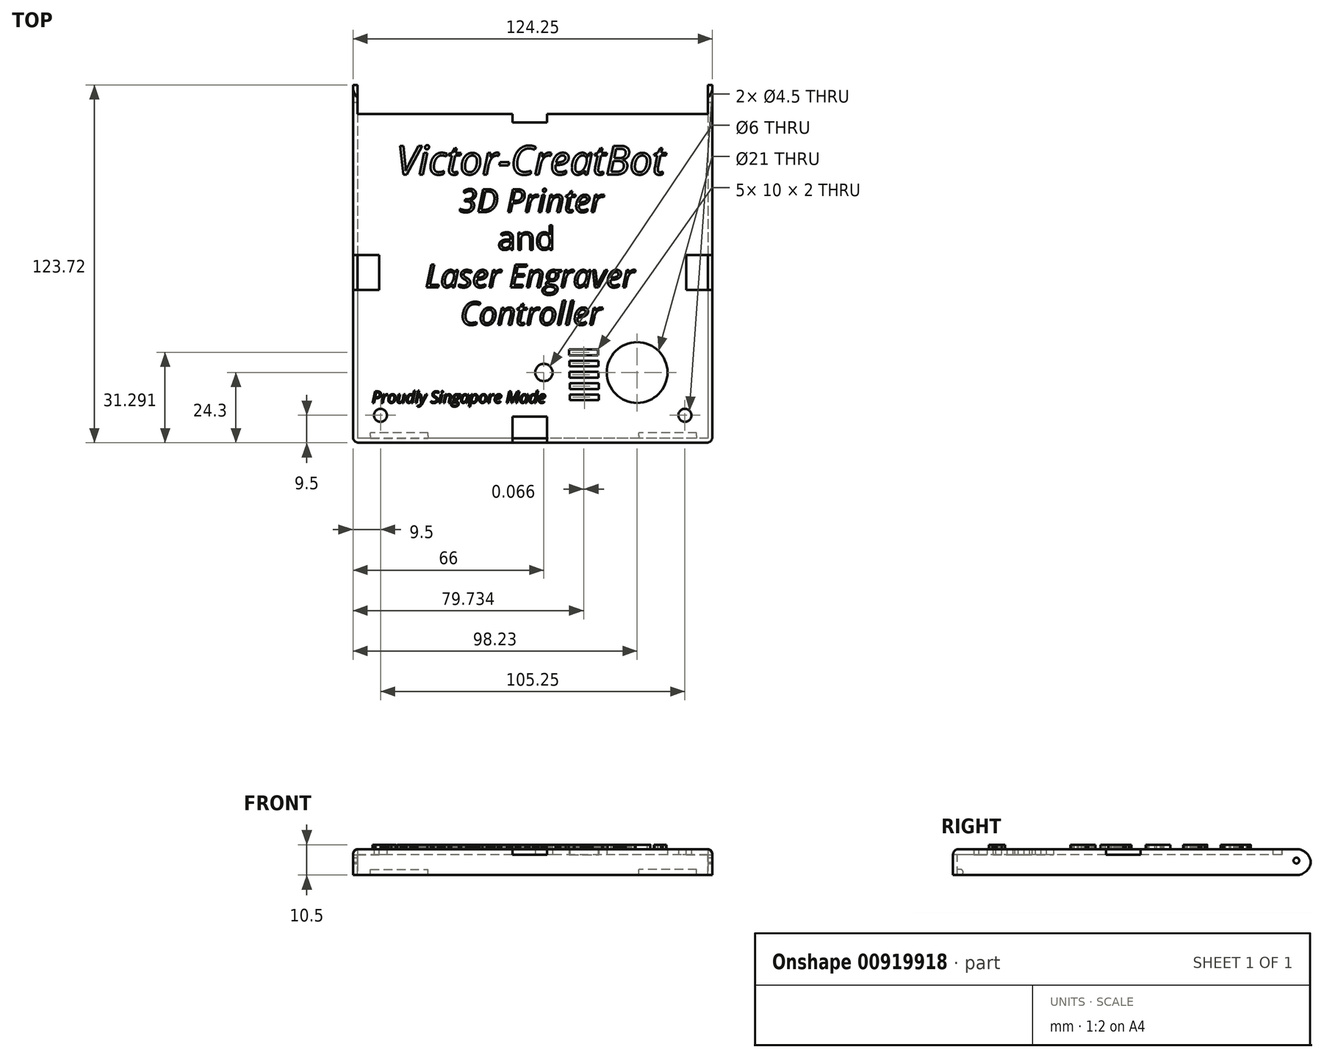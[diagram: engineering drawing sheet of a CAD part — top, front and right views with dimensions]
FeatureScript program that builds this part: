
annotation { "Feature Type Name" : "Feature", "Feature Type Description" : "" }
export const myFeature = defineFeature(function(context is Context, id is Id, definition is map)
    precondition{}
    {
        {
            var Q0;
            Q0=qCreatedBy(makeId("Top.planeOp"),FACE);
            var sketch = newSketch(context, id + "F0", { "sketchPlane" : qUnion([Q0])});
            skLineSegment(sketch, "E0.bottom", {"start": v(0, 0) * mm, "end": v(112.25, 0) * mm});
            skLineSegment(sketch, "E0.top", {"start": v(0, 107.75) * mm, "end": v(112.25, 107.75) * mm});
            skLineSegment(sketch, "E0.left", {"start": v(0, 0) * mm, "end": v(0, 107.75) * mm});
            skLineSegment(sketch, "E0.right", {"start": v(112.25, 0) * mm, "end": v(112.25, 107.75) * mm});
            skCircle(sketch, "E1", {"center": v(3.5, 3.5) * mm, "radius": 2.25 * mm});
            skCircle(sketch, "E2", {"center": v(108.75, 3.5) * mm, "radius": 2.25 * mm});
            skCircle(sketch, "E3", {"center": v(92.23, 18.3) * mm, "radius": 10.5 * mm});
            skCircle(sketch, "E4", {"center": v(60, 18.3) * mm, "radius": 3 * mm});
            skLineSegment(sketch, "E5.bottom", {"start": v(68.73, 26.3) * mm, "end": v(78.73, 26.3) * mm});
            skLineSegment(sketch, "E5.top", {"start": v(68.73, 24.3) * mm, "end": v(78.73, 24.3) * mm});
            skLineSegment(sketch, "E5.left", {"start": v(68.73, 26.3) * mm, "end": v(68.73, 24.3) * mm});
            skLineSegment(sketch, "E5.right", {"start": v(78.73, 26.3) * mm, "end": v(78.73, 24.3) * mm});
            skLineSegment(sketch, "E6.1.0.0", {"start": v(78.8, 22.4) * mm, "end": v(78.8, 20.4) * mm});
            skLineSegment(sketch, "E6.1.0.1", {"start": v(68.8, 22.4) * mm, "end": v(68.8, 20.4) * mm});
            skLineSegment(sketch, "E6.1.0.2", {"start": v(68.8, 22.4) * mm, "end": v(78.8, 22.4) * mm});
            skLineSegment(sketch, "E6.1.0.3", {"start": v(68.8, 20.4) * mm, "end": v(78.8, 20.4) * mm});
            skLineSegment(sketch, "E6.2.0.0", {"start": v(78.87, 18.5) * mm, "end": v(78.87, 16.5) * mm});
            skLineSegment(sketch, "E6.2.0.1", {"start": v(68.87, 18.5) * mm, "end": v(68.87, 16.5) * mm});
            skLineSegment(sketch, "E6.2.0.2", {"start": v(68.87, 18.5) * mm, "end": v(78.87, 18.5) * mm});
            skLineSegment(sketch, "E6.2.0.3", {"start": v(68.87, 16.5) * mm, "end": v(78.87, 16.5) * mm});
            skLineSegment(sketch, "E6.3.0.0", {"start": v(78.93, 14.62) * mm, "end": v(78.93, 12.62) * mm});
            skLineSegment(sketch, "E6.3.0.1", {"start": v(68.93, 14.62) * mm, "end": v(68.93, 12.62) * mm});
            skLineSegment(sketch, "E6.3.0.2", {"start": v(68.93, 14.62) * mm, "end": v(78.93, 14.62) * mm});
            skLineSegment(sketch, "E6.3.0.3", {"start": v(68.93, 12.62) * mm, "end": v(78.93, 12.62) * mm});
            skLineSegment(sketch, "E6.4.0.0", {"start": v(79, 10.73) * mm, "end": v(79, 8.73) * mm});
            skLineSegment(sketch, "E6.4.0.1", {"start": v(69, 10.73) * mm, "end": v(69, 8.73) * mm});
            skLineSegment(sketch, "E6.4.0.2", {"start": v(69, 10.73) * mm, "end": v(79, 10.73) * mm});
            skLineSegment(sketch, "E6.4.0.3", {"start": v(69, 8.73) * mm, "end": v(79, 8.73) * mm});
            skLineSegment(sketch, "E6.direction1", {"start": v(68.73, 24.3) * mm, "end": v(68.8, 20.4) * mm, "construction": true});
            skSolve(sketch);
        }
        {
            var Q0;
            Q0=qSketchRegion(id+"F0",true);
            extrude(context, id + "F1", {"entities" : qUnion([Q0]), "depth" : 2 * mm, "offsetDistance" : 25 * mm});
        }
        {
            var Q0;
            Q0=makeQuery(id+"F1.opExtrude","CAP_FACE",FACE,{"disambiguationData":[OSD([sQuery(id+"F0.wireOp",EDGE,"E0.bottom"),sQuery(id+"F0.wireOp",EDGE,"E0.top"),sQuery(id+"F0.wireOp",EDGE,"E0.left"),sQuery(id+"F0.wireOp",EDGE,"E0.right"),sQuery(id+"F0.wireOp",EDGE,"VJWhoFmN-CNNd-a6gC-JCuR-XAWFigalHExP"),sQuery(id+"F0.wireOp",EDGE,"vIjKD9R8-VXcQ-Syzh-FnhK-4sEpH6Cil4JO"),sQuery(id+"F0.wireOp",EDGE,"E1"),sQuery(id+"F0.wireOp",EDGE,"E2"),sQuery(id+"F0.wireOp",EDGE,"RQaqiYP4-0Fcv-lfBv-gB3g-qDtZXz7Vt3Ng.bottom"),sQuery(id+"F0.wireOp",EDGE,"RQaqiYP4-0Fcv-lfBv-gB3g-qDtZXz7Vt3Ng.top"),sQuery(id+"F0.wireOp",EDGE,"RQaqiYP4-0Fcv-lfBv-gB3g-qDtZXz7Vt3Ng.left"),sQuery(id+"F0.wireOp",EDGE,"RQaqiYP4-0Fcv-lfBv-gB3g-qDtZXz7Vt3Ng.right"),sQuery(id+"F0.wireOp",EDGE,"E3"),sQuery(id+"F0.wireOp",EDGE,"E4"),sQuery(id+"F0.wireOp",EDGE,"A4T1cfBq-erl5-skMh-XZ60-SgpOEBQzwWt8"),sQuery(id+"F0.wireOp",EDGE,"E5.bottom"),sQuery(id+"F0.wireOp",EDGE,"E5.top"),sQuery(id+"F0.wireOp",EDGE,"E5.left"),sQuery(id+"F0.wireOp",EDGE,"E5.right"),sQuery(id+"F0.wireOp",EDGE,"E6.1.0.0"),sQuery(id+"F0.wireOp",EDGE,"E6.1.0.1"),sQuery(id+"F0.wireOp",EDGE,"E6.1.0.2"),sQuery(id+"F0.wireOp",EDGE,"E6.1.0.3"),sQuery(id+"F0.wireOp",EDGE,"E6.2.0.0"),sQuery(id+"F0.wireOp",EDGE,"E6.2.0.1"),sQuery(id+"F0.wireOp",EDGE,"E6.2.0.2"),sQuery(id+"F0.wireOp",EDGE,"E6.2.0.3"),sQuery(id+"F0.wireOp",EDGE,"E6.3.0.0"),sQuery(id+"F0.wireOp",EDGE,"E6.3.0.1"),sQuery(id+"F0.wireOp",EDGE,"E6.3.0.2"),sQuery(id+"F0.wireOp",EDGE,"E6.3.0.3"),sQuery(id+"F0.wireOp",EDGE,"E6.4.0.0"),sQuery(id+"F0.wireOp",EDGE,"E6.4.0.1"),sQuery(id+"F0.wireOp",EDGE,"E6.4.0.2"),sQuery(id+"F0.wireOp",EDGE,"E6.4.0.3")])],"isStart":false});
            var sketch = newSketch(context, id + "F2", { "sketchPlane" : qUnion([Q0])});
            skLineSegment(sketch, "E7.bottom", {"start": v(109.25, 58.87) * mm, "end": v(115.25, 58.87) * mm});
            skLineSegment(sketch, "E7.top", {"start": v(109.25, 46.87) * mm, "end": v(115.25, 46.87) * mm});
            skLineSegment(sketch, "E7.left", {"start": v(109.25, 58.87) * mm, "end": v(109.25, 46.87) * mm});
            skLineSegment(sketch, "E7.right", {"start": v(115.25, 58.87) * mm, "end": v(115.25, 46.87) * mm});
            skLineSegment(sketch, "E8.bottom", {"start": v(-3, 58.87) * mm, "end": v(3, 58.87) * mm});
            skLineSegment(sketch, "E8.top", {"start": v(-3, 46.87) * mm, "end": v(3, 46.87) * mm});
            skLineSegment(sketch, "E8.left", {"start": v(-3, 58.87) * mm, "end": v(-3, 46.87) * mm});
            skLineSegment(sketch, "E8.right", {"start": v(3, 58.87) * mm, "end": v(3, 46.87) * mm});
            skLineSegment(sketch, "E9.bottom", {"start": v(49.13, 110.75) * mm, "end": v(61.13, 110.75) * mm});
            skLineSegment(sketch, "E9.top", {"start": v(49.13, 104.75) * mm, "end": v(61.13, 104.75) * mm});
            skLineSegment(sketch, "E9.left", {"start": v(49.13, 110.75) * mm, "end": v(49.13, 104.75) * mm});
            skLineSegment(sketch, "E9.right", {"start": v(61.13, 110.75) * mm, "end": v(61.13, 104.75) * mm});
            skLineSegment(sketch, "E10.bottom", {"start": v(49.13, 3) * mm, "end": v(61.13, 3) * mm});
            skLineSegment(sketch, "E10.top", {"start": v(49.13, -3) * mm, "end": v(61.13, -3) * mm});
            skLineSegment(sketch, "E10.left", {"start": v(49.13, 3) * mm, "end": v(49.13, -3) * mm});
            skLineSegment(sketch, "E10.right", {"start": v(61.13, 3) * mm, "end": v(61.13, -3) * mm});
            skSolve(sketch);
        }
        {
            var Q0;
            Q0=qSketchRegion(id+"F2",true);
            extrude(context, id + "F3", {"entities" : qUnion([Q0]), "operationType" : NewBodyOperationType.REMOVE, "endBound" : BoundingType.THROUGH_ALL, "oppositeDirection" : true, "depth" : 3 * mm, "offsetDistance" : 25 * mm});
        }
        {
            var Q0;
            {var subQ27=sQuery(id+"F0.wireOp",EDGE,"E0.left");var subQ29=sQuery(id+"F0.wireOp",EDGE,"E0.bottom");Q0=makeQuery(id+"F3.boolean.opBoolean","SPLIT",FACE,{"disambiguationData":[TD([makeQuery(id+"F1.opExtrude","SWEPT_FACE",FACE,{"disambiguationData":[OSD([subQ27])]})])],"derivedFrom":makeQuery(id+"F1.opExtrude","SWEPT_FACE",FACE,{"disambiguationData":[OSD([subQ29])]})});}
            var Q1;
            {var subQ26=sQuery(id+"F0.wireOp",EDGE,"E0.right");var subQ29=sQuery(id+"F0.wireOp",EDGE,"E0.bottom");Q1=makeQuery(id+"F3.boolean.opBoolean","SPLIT",FACE,{"disambiguationData":[TD([makeQuery(id+"F1.opExtrude","SWEPT_FACE",FACE,{"disambiguationData":[OSD([subQ26])]})])],"derivedFrom":makeQuery(id+"F1.opExtrude","SWEPT_FACE",FACE,{"disambiguationData":[OSD([subQ29])]})});}
            extrude(context, id + "F4", {"entities" : qUnion([Q0, Q1]), "operationType" : NewBodyOperationType.ADD, "depth" : 6 * mm, "offsetDistance" : 25 * mm});
        }
        {
            var Q0;
            {var subQ27=sQuery(id+"F0.wireOp",EDGE,"E0.left");var subQ28=sQuery(id+"F0.wireOp",EDGE,"E0.top");Q0=makeQuery(id+"F3.boolean.opBoolean","SPLIT",FACE,{"disambiguationData":[TD([makeQuery(id+"F1.opExtrude","SWEPT_FACE",FACE,{"disambiguationData":[OSD([subQ28])]})])],"derivedFrom":makeQuery(id+"F1.opExtrude","SWEPT_FACE",FACE,{"disambiguationData":[OSD([subQ27])]})});}
            var Q1;
            {var subQ0=sQuery(id+"F0.wireOp",EDGE,"E0.left");var subQ1=sQuery(id+"F0.wireOp",EDGE,"E0.bottom");Q1=makeQuery(id+"F4.boolean.opBoolean","MERGE",FACE,{"derivedFrom":[makeQuery(id+"F3.boolean.opBoolean","SPLIT",FACE,{"disambiguationData":[TD([makeQuery(id+"F1.opExtrude","SWEPT_FACE",FACE,{"disambiguationData":[OSD([subQ1])]})])],"derivedFrom":makeQuery(id+"F1.opExtrude","SWEPT_FACE",FACE,{"disambiguationData":[OSD([subQ0])]})}),makeQuery(id+"F4.opExtrude","SWEPT_FACE",FACE,{"disambiguationData":[OSD([subQ1,subQ0])]})]});}
            extrude(context, id + "F5", {"entities" : qUnion([Q0, Q1]), "operationType" : NewBodyOperationType.ADD, "depth" : 6 * mm, "offsetDistance" : 25 * mm});
        }
        {
            var Q0;
            {var subQ26=sQuery(id+"F0.wireOp",EDGE,"E0.right");var subQ28=sQuery(id+"F0.wireOp",EDGE,"E0.top");Q0=makeQuery(id+"F3.boolean.opBoolean","SPLIT",FACE,{"disambiguationData":[TD([makeQuery(id+"F1.opExtrude","SWEPT_FACE",FACE,{"disambiguationData":[OSD([subQ28])]})])],"derivedFrom":makeQuery(id+"F1.opExtrude","SWEPT_FACE",FACE,{"disambiguationData":[OSD([subQ26])]})});}
            var Q1;
            {var subQ0=sQuery(id+"F0.wireOp",EDGE,"E0.right");var subQ1=sQuery(id+"F0.wireOp",EDGE,"E0.bottom");Q1=makeQuery(id+"F4.boolean.opBoolean","MERGE",FACE,{"derivedFrom":[makeQuery(id+"F3.boolean.opBoolean","SPLIT",FACE,{"disambiguationData":[TD([makeQuery(id+"F1.opExtrude","SWEPT_FACE",FACE,{"disambiguationData":[OSD([subQ1])]})])],"derivedFrom":makeQuery(id+"F1.opExtrude","SWEPT_FACE",FACE,{"disambiguationData":[OSD([subQ0])]})}),makeQuery(id+"F4.opExtrude","SWEPT_FACE",FACE,{"disambiguationData":[OSD([subQ1,subQ0])]})]});}
            extrude(context, id + "F6", {"entities" : qUnion([Q0, Q1]), "operationType" : NewBodyOperationType.ADD, "depth" : 6 * mm, "offsetDistance" : 25 * mm});
        }
        {
            var Q0;
            {var subQ0=sQuery(id+"F0.wireOp",EDGE,"E0.right");var subQ1=sQuery(id+"F0.wireOp",EDGE,"E0.bottom");var subQ2=makeQuery(id+"F1.opExtrude","SWEPT_FACE",FACE,{"disambiguationData":[OSD([subQ1])]});var subQ3=makeQuery(id+"F1.opExtrude","SWEPT_FACE",FACE,{"disambiguationData":[OSD([subQ0])]});var subQ4=sQuery(id+"F0.wireOp",EDGE,"E0.left");var subQ5=sQuery(id+"F0.wireOp",EDGE,"E0.top");var subQ6=makeQuery(id+"F1.opExtrude","CAP_FACE",FACE,{"disambiguationData":[OSD([subQ1,subQ5,subQ4,subQ0,sQuery(id+"F0.wireOp",EDGE,"VJWhoFmN-CNNd-a6gC-JCuR-XAWFigalHExP"),sQuery(id+"F0.wireOp",EDGE,"vIjKD9R8-VXcQ-Syzh-FnhK-4sEpH6Cil4JO"),sQuery(id+"F0.wireOp",EDGE,"E1"),sQuery(id+"F0.wireOp",EDGE,"E2"),sQuery(id+"F0.wireOp",EDGE,"E3"),sQuery(id+"F0.wireOp",EDGE,"E4"),sQuery(id+"F0.wireOp",EDGE,"E5.bottom"),sQuery(id+"F0.wireOp",EDGE,"E5.top"),sQuery(id+"F0.wireOp",EDGE,"E5.left"),sQuery(id+"F0.wireOp",EDGE,"E5.right"),sQuery(id+"F0.wireOp",EDGE,"E6.1.0.0"),sQuery(id+"F0.wireOp",EDGE,"E6.1.0.1"),sQuery(id+"F0.wireOp",EDGE,"E6.1.0.2"),sQuery(id+"F0.wireOp",EDGE,"E6.1.0.3"),sQuery(id+"F0.wireOp",EDGE,"E6.2.0.0"),sQuery(id+"F0.wireOp",EDGE,"E6.2.0.1"),sQuery(id+"F0.wireOp",EDGE,"E6.2.0.2"),sQuery(id+"F0.wireOp",EDGE,"E6.2.0.3"),sQuery(id+"F0.wireOp",EDGE,"E6.3.0.0"),sQuery(id+"F0.wireOp",EDGE,"E6.3.0.1"),sQuery(id+"F0.wireOp",EDGE,"E6.3.0.2"),sQuery(id+"F0.wireOp",EDGE,"E6.3.0.3"),sQuery(id+"F0.wireOp",EDGE,"E6.4.0.0"),sQuery(id+"F0.wireOp",EDGE,"E6.4.0.1"),sQuery(id+"F0.wireOp",EDGE,"E6.4.0.2"),sQuery(id+"F0.wireOp",EDGE,"E6.4.0.3")])],"isStart":true});var subQ7=makeQuery(id+"F1.opExtrude","CAP_EDGE",EDGE,{"disambiguationData":[OSD([subQ0])],"isStart":true});var subQ8=makeQuery(id+"F1.opExtrude","SWEPT_FACE",FACE,{"disambiguationData":[OSD([subQ5])]});var subQ9=makeQuery(id+"F1.opExtrude","SWEPT_FACE",FACE,{"disambiguationData":[OSD([subQ4])]});var subQ10=makeQuery(id+"F1.opExtrude","CAP_EDGE",EDGE,{"disambiguationData":[OSD([subQ4])],"isStart":true});var subQ11=makeQuery(id+"F1.opExtrude","CAP_EDGE",EDGE,{"disambiguationData":[OSD([subQ1])],"isStart":true});Q0=makeQuery(id+"F6.boolean.opBoolean","MERGE",FACE,{"derivedFrom":[makeQuery(id+"F5.boolean.opBoolean","MERGE",FACE,{"derivedFrom":[makeQuery(id+"F4.boolean.opBoolean","MERGE",FACE,{"derivedFrom":[subQ6,makeQuery(id+"F4.opExtrude","SWEPT_FACE",FACE,{"disambiguationData":[OSD([subQ1]),TDD([makeQuery(id+"F3.boolean.opBoolean","SPLIT",EDGE,{"disambiguationData":[TD([subQ9])],"derivedFrom":subQ11})])]}),makeQuery(id+"F4.opExtrude","SWEPT_FACE",FACE,{"disambiguationData":[OSD([subQ1]),TDD([makeQuery(id+"F3.boolean.opBoolean","SPLIT",EDGE,{"disambiguationData":[TD([subQ3])],"derivedFrom":subQ11})])]})]}),makeQuery(id+"F5.opExtrude","SWEPT_FACE",FACE,{"disambiguationData":[OSD([subQ4]),TDD([makeQuery(id+"F3.boolean.opBoolean","SPLIT",EDGE,{"disambiguationData":[TD([subQ8])],"derivedFrom":subQ10})])]}),makeQuery(id+"F5.opExtrude","SWEPT_FACE",FACE,{"disambiguationData":[OSD([subQ1,subQ4]),TDD([makeQuery(id+"F4.boolean.opBoolean","MERGE",EDGE,{"derivedFrom":[makeQuery(id+"F3.boolean.opBoolean","SPLIT",EDGE,{"disambiguationData":[TD([subQ2])],"derivedFrom":subQ10}),makeQuery(id+"F4.opExtrude","SWEPT_EDGE",EDGE,{"disambiguationData":[OSD([subQ1,subQ4]),TDD([makeQuery(id+"F1.opExtrude","CAP_VERTEX",VERTEX,{"disambiguationData":[OSD([subQ1,subQ4])],"isStart":true})])]})]})])]})]}),makeQuery(id+"F6.opExtrude","SWEPT_FACE",FACE,{"disambiguationData":[OSD([subQ0]),TDD([makeQuery(id+"F3.boolean.opBoolean","SPLIT",EDGE,{"disambiguationData":[TD([subQ8])],"derivedFrom":subQ7})])]}),makeQuery(id+"F6.opExtrude","SWEPT_FACE",FACE,{"disambiguationData":[OSD([subQ1,subQ0]),TDD([makeQuery(id+"F4.boolean.opBoolean","MERGE",EDGE,{"derivedFrom":[makeQuery(id+"F3.boolean.opBoolean","SPLIT",EDGE,{"disambiguationData":[TD([subQ2])],"derivedFrom":subQ7}),makeQuery(id+"F4.opExtrude","SWEPT_EDGE",EDGE,{"disambiguationData":[OSD([subQ1,subQ0]),TDD([makeQuery(id+"F1.opExtrude","CAP_VERTEX",VERTEX,{"disambiguationData":[OSD([subQ1,subQ0])],"isStart":true})])]})]})])]})]});}
            var sketch = newSketch(context, id + "F7", { "sketchPlane" : qUnion([Q0])});
            skLineSegment(sketch, "E11.bottom", {"start": v(118.25, -107.75) * mm, "end": v(116.75, -107.75) * mm});
            skLineSegment(sketch, "E11.top", {"start": v(118.25, 6) * mm, "end": v(116.75, 6) * mm});
            skLineSegment(sketch, "E11.left", {"start": v(118.25, -107.75) * mm, "end": v(118.25, -58.87) * mm});
            skLineSegment(sketch, "E11.right", {"start": v(116.75, -107.75) * mm, "end": v(116.75, -58.87) * mm});
            skLineSegment(sketch, "E12.bottom", {"start": v(-6, -107.75) * mm, "end": v(-4.5, -107.75) * mm});
            skLineSegment(sketch, "E12.top", {"start": v(-6, 6) * mm, "end": v(-4.5, 6) * mm});
            skLineSegment(sketch, "E12.left", {"start": v(-6, -107.75) * mm, "end": v(-6, -58.87) * mm});
            skLineSegment(sketch, "E12.right", {"start": v(-4.5, -107.75) * mm, "end": v(-4.5, -58.87) * mm});
            skLineSegment(sketch, "E13.bottom", {"start": v(116.75, 4.5) * mm, "end": v(61.13, 4.5) * mm});
            skLineSegment(sketch, "E13.top", {"start": v(116.75, 6) * mm, "end": v(61.13, 6) * mm});
            skLineSegment(sketch, "E14.trimOffspring", {"start": v(61.13, 4.5) * mm, "end": v(-4.5, 4.5) * mm});
            skLineSegment(sketch, "E15.trimOffspring", {"start": v(61.13, 6) * mm, "end": v(-4.5, 6) * mm});
            skLineSegment(sketch, "E16.trimOffspring", {"start": v(118.25, -58.87) * mm, "end": v(118.25, 6) * mm});
            skLineSegment(sketch, "E17.trimOffspring", {"start": v(116.75, -58.87) * mm, "end": v(116.75, 4.5) * mm});
            skLineSegment(sketch, "E18.trimOffspring", {"start": v(-4.5, -58.87) * mm, "end": v(-4.5, 4.5) * mm});
            skLineSegment(sketch, "E19.trimOffspring", {"start": v(-6, -58.87) * mm, "end": v(-6, 6) * mm});
            skSolve(sketch);
        }
        {
            var Q0;
            {var subQ43=sQuery(id+"F7.wireOp",EDGE,"E12.top");Q0=makeQuery(id+"F7.imprint","IMPRINT",FACE,{"disambiguationData":[TD([[makeQuery(id+"F7.imprint","IMPRINT",EDGE,{"derivedFrom":subQ43}),-1.0]])]});}
            var Q1;
            {var subQ0=sQuery(id+"F7.wireOp",EDGE,"E14.trimOffspring");var subQ2=sQuery(id+"F0.wireOp",EDGE,"E6.4.0.3");var subQ3=sQuery(id+"F0.wireOp",EDGE,"E6.4.0.2");var subQ4=sQuery(id+"F0.wireOp",EDGE,"E6.4.0.1");var subQ5=sQuery(id+"F0.wireOp",EDGE,"E6.4.0.0");var subQ6=sQuery(id+"F0.wireOp",EDGE,"E6.3.0.3");var subQ7=sQuery(id+"F0.wireOp",EDGE,"E6.3.0.2");var subQ8=sQuery(id+"F0.wireOp",EDGE,"E6.3.0.1");var subQ9=sQuery(id+"F0.wireOp",EDGE,"E6.3.0.0");var subQ10=sQuery(id+"F0.wireOp",EDGE,"E6.2.0.3");var subQ11=sQuery(id+"F0.wireOp",EDGE,"E6.2.0.2");var subQ12=sQuery(id+"F0.wireOp",EDGE,"E6.2.0.1");var subQ13=sQuery(id+"F0.wireOp",EDGE,"E6.2.0.0");var subQ14=sQuery(id+"F0.wireOp",EDGE,"E6.1.0.3");var subQ15=sQuery(id+"F0.wireOp",EDGE,"E6.1.0.2");var subQ16=sQuery(id+"F0.wireOp",EDGE,"E6.1.0.1");var subQ17=sQuery(id+"F0.wireOp",EDGE,"E6.1.0.0");var subQ18=sQuery(id+"F0.wireOp",EDGE,"E5.right");var subQ19=sQuery(id+"F0.wireOp",EDGE,"E5.left");var subQ20=sQuery(id+"F0.wireOp",EDGE,"E5.top");var subQ21=sQuery(id+"F0.wireOp",EDGE,"E5.bottom");var subQ22=sQuery(id+"F0.wireOp",EDGE,"E4");var subQ23=sQuery(id+"F0.wireOp",EDGE,"E3");var subQ24=sQuery(id+"F0.wireOp",EDGE,"E2");var subQ25=sQuery(id+"F0.wireOp",EDGE,"E1");var subQ26=sQuery(id+"F0.wireOp",EDGE,"vIjKD9R8-VXcQ-Syzh-FnhK-4sEpH6Cil4JO");var subQ27=sQuery(id+"F0.wireOp",EDGE,"VJWhoFmN-CNNd-a6gC-JCuR-XAWFigalHExP");var subQ28=sQuery(id+"F0.wireOp",EDGE,"E0.right");var subQ29=sQuery(id+"F0.wireOp",EDGE,"E0.left");var subQ30=sQuery(id+"F0.wireOp",EDGE,"E0.top");var subQ31=sQuery(id+"F0.wireOp",EDGE,"E0.bottom");var subQ32=makeQuery(id+"F1.opExtrude","CAP_FACE",FACE,{"disambiguationData":[OSD([subQ31,subQ30,subQ29,subQ28,subQ27,subQ26,subQ25,subQ24,subQ23,subQ22,subQ21,subQ20,subQ19,subQ18,subQ17,subQ16,subQ15,subQ14,subQ13,subQ12,subQ11,subQ10,subQ9,subQ8,subQ7,subQ6,subQ5,subQ4,subQ3,subQ2])],"isStart":true});var subQ35=sQuery(id+"F2.wireOp",EDGE,"E10.left");var subQ36=makeQuery(id+"F4.boolean.opBoolean","MERGE",EDGE,{"derivedFrom":[makeQuery(id+"F3.boolean.opBoolean","INTERSECT",EDGE,{"derivedFrom":[subQ32,makeQuery(id+"F3.opExtrude","SWEPT_FACE",FACE,{"disambiguationData":[OSD([subQ35])]})]}),makeQuery(id+"F4.opExtrude","SWEPT_EDGE",EDGE,{"disambiguationData":[OSD([subQ31,subQ30,subQ29,subQ28,subQ27,subQ26,subQ25,subQ24,subQ23,subQ22,subQ21,subQ20,subQ19,subQ18,subQ17,subQ16,subQ15,subQ14,subQ13,subQ12,subQ11,subQ10,subQ9,subQ8,subQ7,subQ6,subQ5,subQ4,subQ3,subQ2,subQ35])]})]});var subQ37=makeQuery(id+"F7.imprint","INTERSECT",VERTEX,{"derivedFrom":[subQ36,subQ0]});Q1=makeQuery(id+"F7.imprint","IMPRINT",FACE,{"disambiguationData":[TD([[makeQuery(id+"F7.imprint","IMPRINT",EDGE,{"disambiguationData":[TD([[subQ37,1.0]])],"derivedFrom":subQ0}),-1.0]])]});}
            var Q2;
            {var subQ35=sQuery(id+"F7.wireOp",EDGE,"E11.top");Q2=makeQuery(id+"F7.imprint","IMPRINT",FACE,{"disambiguationData":[TD([[makeQuery(id+"F7.imprint","IMPRINT",EDGE,{"derivedFrom":subQ35}),-1.0]])]});}
            var Q3;
            {var subQ0=sQuery(id+"F7.wireOp",EDGE,"E18.trimOffspring");var subQ2=sQuery(id+"F0.wireOp",EDGE,"E6.4.0.3");var subQ3=sQuery(id+"F0.wireOp",EDGE,"E6.4.0.2");var subQ4=sQuery(id+"F0.wireOp",EDGE,"E6.4.0.1");var subQ5=sQuery(id+"F0.wireOp",EDGE,"E6.4.0.0");var subQ6=sQuery(id+"F0.wireOp",EDGE,"E6.3.0.3");var subQ7=sQuery(id+"F0.wireOp",EDGE,"E6.3.0.2");var subQ8=sQuery(id+"F0.wireOp",EDGE,"E6.3.0.1");var subQ9=sQuery(id+"F0.wireOp",EDGE,"E6.3.0.0");var subQ10=sQuery(id+"F0.wireOp",EDGE,"E6.2.0.3");var subQ11=sQuery(id+"F0.wireOp",EDGE,"E6.2.0.2");var subQ12=sQuery(id+"F0.wireOp",EDGE,"E6.2.0.1");var subQ13=sQuery(id+"F0.wireOp",EDGE,"E6.2.0.0");var subQ14=sQuery(id+"F0.wireOp",EDGE,"E6.1.0.3");var subQ15=sQuery(id+"F0.wireOp",EDGE,"E6.1.0.2");var subQ16=sQuery(id+"F0.wireOp",EDGE,"E6.1.0.1");var subQ17=sQuery(id+"F0.wireOp",EDGE,"E6.1.0.0");var subQ18=sQuery(id+"F0.wireOp",EDGE,"E5.right");var subQ19=sQuery(id+"F0.wireOp",EDGE,"E5.left");var subQ20=sQuery(id+"F0.wireOp",EDGE,"E5.top");var subQ21=sQuery(id+"F0.wireOp",EDGE,"E5.bottom");var subQ22=sQuery(id+"F0.wireOp",EDGE,"E4");var subQ23=sQuery(id+"F0.wireOp",EDGE,"E3");var subQ24=sQuery(id+"F0.wireOp",EDGE,"E2");var subQ25=sQuery(id+"F0.wireOp",EDGE,"E1");var subQ26=sQuery(id+"F0.wireOp",EDGE,"vIjKD9R8-VXcQ-Syzh-FnhK-4sEpH6Cil4JO");var subQ27=sQuery(id+"F0.wireOp",EDGE,"VJWhoFmN-CNNd-a6gC-JCuR-XAWFigalHExP");var subQ28=sQuery(id+"F0.wireOp",EDGE,"E0.right");var subQ29=sQuery(id+"F0.wireOp",EDGE,"E0.left");var subQ30=sQuery(id+"F0.wireOp",EDGE,"E0.top");var subQ31=sQuery(id+"F0.wireOp",EDGE,"E0.bottom");var subQ32=makeQuery(id+"F1.opExtrude","CAP_FACE",FACE,{"disambiguationData":[OSD([subQ31,subQ30,subQ29,subQ28,subQ27,subQ26,subQ25,subQ24,subQ23,subQ22,subQ21,subQ20,subQ19,subQ18,subQ17,subQ16,subQ15,subQ14,subQ13,subQ12,subQ11,subQ10,subQ9,subQ8,subQ7,subQ6,subQ5,subQ4,subQ3,subQ2])],"isStart":true});var subQ35=sQuery(id+"F2.wireOp",EDGE,"E8.top");var subQ36=makeQuery(id+"F5.boolean.opBoolean","MERGE",EDGE,{"derivedFrom":[makeQuery(id+"F3.boolean.opBoolean","INTERSECT",EDGE,{"derivedFrom":[subQ32,makeQuery(id+"F3.opExtrude","SWEPT_FACE",FACE,{"disambiguationData":[OSD([subQ35])]})]}),makeQuery(id+"F5.opExtrude","SWEPT_EDGE",EDGE,{"disambiguationData":[OSD([subQ31,subQ30,subQ29,subQ28,subQ27,subQ26,subQ25,subQ24,subQ23,subQ22,subQ21,subQ20,subQ19,subQ18,subQ17,subQ16,subQ15,subQ14,subQ13,subQ12,subQ11,subQ10,subQ9,subQ8,subQ7,subQ6,subQ5,subQ4,subQ3,subQ2,subQ35])]})]});var subQ37=makeQuery(id+"F7.imprint","INTERSECT",VERTEX,{"derivedFrom":[subQ36,subQ0]});Q3=makeQuery(id+"F7.imprint","IMPRINT",FACE,{"disambiguationData":[TD([[makeQuery(id+"F7.imprint","IMPRINT",EDGE,{"disambiguationData":[TD([[subQ37,1.0]])],"derivedFrom":subQ0}),1.0]])]});}
            var Q4;
            Q4=makeQuery(id+"F7.imprint","IMPRINT",FACE,{"disambiguationData":[TD([[makeQuery(id+"F7.imprint","IMPRINT",EDGE,{"derivedFrom":sQuery(id+"F7.wireOp",EDGE,"E12.bottom")}),1.0]])]});
            var Q5;
            {var subQ0=sQuery(id+"F7.wireOp",EDGE,"E16.trimOffspring");var subQ1=sQuery(id+"F2.wireOp",EDGE,"E7.bottom");var subQ2=sQuery(id+"F0.wireOp",EDGE,"E6.4.0.3");var subQ3=sQuery(id+"F0.wireOp",EDGE,"E6.4.0.2");var subQ4=sQuery(id+"F0.wireOp",EDGE,"E6.4.0.1");var subQ5=sQuery(id+"F0.wireOp",EDGE,"E6.4.0.0");var subQ6=sQuery(id+"F0.wireOp",EDGE,"E6.3.0.3");var subQ7=sQuery(id+"F0.wireOp",EDGE,"E6.3.0.2");var subQ8=sQuery(id+"F0.wireOp",EDGE,"E6.3.0.1");var subQ9=sQuery(id+"F0.wireOp",EDGE,"E6.3.0.0");var subQ10=sQuery(id+"F0.wireOp",EDGE,"E6.2.0.3");var subQ11=sQuery(id+"F0.wireOp",EDGE,"E6.2.0.2");var subQ12=sQuery(id+"F0.wireOp",EDGE,"E6.2.0.1");var subQ13=sQuery(id+"F0.wireOp",EDGE,"E6.2.0.0");var subQ14=sQuery(id+"F0.wireOp",EDGE,"E6.1.0.3");var subQ15=sQuery(id+"F0.wireOp",EDGE,"E6.1.0.2");var subQ16=sQuery(id+"F0.wireOp",EDGE,"E6.1.0.1");var subQ17=sQuery(id+"F0.wireOp",EDGE,"E6.1.0.0");var subQ18=sQuery(id+"F0.wireOp",EDGE,"E5.right");var subQ19=sQuery(id+"F0.wireOp",EDGE,"E5.left");var subQ20=sQuery(id+"F0.wireOp",EDGE,"E5.top");var subQ21=sQuery(id+"F0.wireOp",EDGE,"E5.bottom");var subQ22=sQuery(id+"F0.wireOp",EDGE,"E4");var subQ23=sQuery(id+"F0.wireOp",EDGE,"E3");var subQ24=sQuery(id+"F0.wireOp",EDGE,"E2");var subQ25=sQuery(id+"F0.wireOp",EDGE,"E1");var subQ26=sQuery(id+"F0.wireOp",EDGE,"vIjKD9R8-VXcQ-Syzh-FnhK-4sEpH6Cil4JO");var subQ27=sQuery(id+"F0.wireOp",EDGE,"VJWhoFmN-CNNd-a6gC-JCuR-XAWFigalHExP");var subQ28=sQuery(id+"F0.wireOp",EDGE,"E0.right");var subQ29=sQuery(id+"F0.wireOp",EDGE,"E0.left");var subQ30=sQuery(id+"F0.wireOp",EDGE,"E0.top");var subQ31=sQuery(id+"F0.wireOp",EDGE,"E0.bottom");var subQ32=makeQuery(id+"F1.opExtrude","CAP_FACE",FACE,{"disambiguationData":[OSD([subQ31,subQ30,subQ29,subQ28,subQ27,subQ26,subQ25,subQ24,subQ23,subQ22,subQ21,subQ20,subQ19,subQ18,subQ17,subQ16,subQ15,subQ14,subQ13,subQ12,subQ11,subQ10,subQ9,subQ8,subQ7,subQ6,subQ5,subQ4,subQ3,subQ2])],"isStart":true});var subQ33=makeQuery(id+"F6.boolean.opBoolean","MERGE",EDGE,{"derivedFrom":[makeQuery(id+"F3.boolean.opBoolean","INTERSECT",EDGE,{"derivedFrom":[subQ32,makeQuery(id+"F3.opExtrude","SWEPT_FACE",FACE,{"disambiguationData":[OSD([subQ1])]})]}),makeQuery(id+"F6.opExtrude","SWEPT_EDGE",EDGE,{"disambiguationData":[OSD([subQ31,subQ30,subQ29,subQ28,subQ27,subQ26,subQ25,subQ24,subQ23,subQ22,subQ21,subQ20,subQ19,subQ18,subQ17,subQ16,subQ15,subQ14,subQ13,subQ12,subQ11,subQ10,subQ9,subQ8,subQ7,subQ6,subQ5,subQ4,subQ3,subQ2,subQ1])]})]});var subQ34=makeQuery(id+"F7.imprint","INTERSECT",VERTEX,{"derivedFrom":[subQ33,sQuery(id+"F7.wireOp",EDGE,"E11.left"),subQ0]});Q5=makeQuery(id+"F7.imprint","IMPRINT",FACE,{"disambiguationData":[TD([[makeQuery(id+"F7.imprint","IMPRINT",EDGE,{"disambiguationData":[TD([[subQ34,-1.0]])],"derivedFrom":subQ0}),1.0]])]});}
            var Q6;
            Q6=makeQuery(id+"F7.imprint","IMPRINT",FACE,{"disambiguationData":[TD([[makeQuery(id+"F7.imprint","IMPRINT",EDGE,{"derivedFrom":sQuery(id+"F7.wireOp",EDGE,"E11.bottom")}),1.0]])]});
            extrude(context, id + "F8", {"entities" : qUnion([Q0, Q1, Q2, Q3, Q4, Q5, Q6]), "operationType" : NewBodyOperationType.ADD, "depth" : 7 * mm, "offsetDistance" : 25 * mm});
        }
        {
            var Q0;
            {var subQ0=sQuery(id+"F0.wireOp",EDGE,"E0.right");var subQ1=sQuery(id+"F0.wireOp",EDGE,"E0.bottom");var subQ2=makeQuery(id+"F1.opExtrude","SWEPT_FACE",FACE,{"disambiguationData":[OSD([subQ1])]});var subQ3=makeQuery(id+"F1.opExtrude","SWEPT_FACE",FACE,{"disambiguationData":[OSD([subQ0])]});var subQ4=sQuery(id+"F0.wireOp",EDGE,"E0.left");var subQ5=sQuery(id+"F0.wireOp",EDGE,"E0.top");var subQ6=makeQuery(id+"F1.opExtrude","CAP_FACE",FACE,{"disambiguationData":[OSD([subQ1,subQ5,subQ4,subQ0,sQuery(id+"F0.wireOp",EDGE,"VJWhoFmN-CNNd-a6gC-JCuR-XAWFigalHExP"),sQuery(id+"F0.wireOp",EDGE,"vIjKD9R8-VXcQ-Syzh-FnhK-4sEpH6Cil4JO"),sQuery(id+"F0.wireOp",EDGE,"E1"),sQuery(id+"F0.wireOp",EDGE,"E2"),sQuery(id+"F0.wireOp",EDGE,"E3"),sQuery(id+"F0.wireOp",EDGE,"E4"),sQuery(id+"F0.wireOp",EDGE,"E5.bottom"),sQuery(id+"F0.wireOp",EDGE,"E5.top"),sQuery(id+"F0.wireOp",EDGE,"E5.left"),sQuery(id+"F0.wireOp",EDGE,"E5.right"),sQuery(id+"F0.wireOp",EDGE,"E6.1.0.0"),sQuery(id+"F0.wireOp",EDGE,"E6.1.0.1"),sQuery(id+"F0.wireOp",EDGE,"E6.1.0.2"),sQuery(id+"F0.wireOp",EDGE,"E6.1.0.3"),sQuery(id+"F0.wireOp",EDGE,"E6.2.0.0"),sQuery(id+"F0.wireOp",EDGE,"E6.2.0.1"),sQuery(id+"F0.wireOp",EDGE,"E6.2.0.2"),sQuery(id+"F0.wireOp",EDGE,"E6.2.0.3"),sQuery(id+"F0.wireOp",EDGE,"E6.3.0.0"),sQuery(id+"F0.wireOp",EDGE,"E6.3.0.1"),sQuery(id+"F0.wireOp",EDGE,"E6.3.0.2"),sQuery(id+"F0.wireOp",EDGE,"E6.3.0.3"),sQuery(id+"F0.wireOp",EDGE,"E6.4.0.0"),sQuery(id+"F0.wireOp",EDGE,"E6.4.0.1"),sQuery(id+"F0.wireOp",EDGE,"E6.4.0.2"),sQuery(id+"F0.wireOp",EDGE,"E6.4.0.3")])],"isStart":false});var subQ7=makeQuery(id+"F1.opExtrude","CAP_EDGE",EDGE,{"disambiguationData":[OSD([subQ0])],"isStart":false});var subQ8=makeQuery(id+"F1.opExtrude","SWEPT_FACE",FACE,{"disambiguationData":[OSD([subQ5])]});var subQ9=makeQuery(id+"F1.opExtrude","SWEPT_FACE",FACE,{"disambiguationData":[OSD([subQ4])]});var subQ10=makeQuery(id+"F1.opExtrude","CAP_EDGE",EDGE,{"disambiguationData":[OSD([subQ4])],"isStart":false});var subQ11=makeQuery(id+"F1.opExtrude","CAP_EDGE",EDGE,{"disambiguationData":[OSD([subQ1])],"isStart":false});Q0=makeQuery(id+"F6.boolean.opBoolean","MERGE",FACE,{"derivedFrom":[makeQuery(id+"F5.boolean.opBoolean","MERGE",FACE,{"derivedFrom":[makeQuery(id+"F4.boolean.opBoolean","MERGE",FACE,{"derivedFrom":[subQ6,makeQuery(id+"F4.opExtrude","SWEPT_FACE",FACE,{"disambiguationData":[OSD([subQ1]),TDD([makeQuery(id+"F3.boolean.opBoolean","SPLIT",EDGE,{"disambiguationData":[TD([subQ9])],"derivedFrom":subQ11})])]}),makeQuery(id+"F4.opExtrude","SWEPT_FACE",FACE,{"disambiguationData":[OSD([subQ1]),TDD([makeQuery(id+"F3.boolean.opBoolean","SPLIT",EDGE,{"disambiguationData":[TD([subQ3])],"derivedFrom":subQ11})])]})]}),makeQuery(id+"F5.opExtrude","SWEPT_FACE",FACE,{"disambiguationData":[OSD([subQ4]),TDD([makeQuery(id+"F3.boolean.opBoolean","SPLIT",EDGE,{"disambiguationData":[TD([subQ8])],"derivedFrom":subQ10})])]}),makeQuery(id+"F5.opExtrude","SWEPT_FACE",FACE,{"disambiguationData":[OSD([subQ1,subQ4]),TDD([makeQuery(id+"F4.boolean.opBoolean","MERGE",EDGE,{"derivedFrom":[makeQuery(id+"F3.boolean.opBoolean","SPLIT",EDGE,{"disambiguationData":[TD([subQ2])],"derivedFrom":subQ10}),makeQuery(id+"F4.opExtrude","SWEPT_EDGE",EDGE,{"disambiguationData":[OSD([subQ1,subQ4]),TDD([makeQuery(id+"F1.opExtrude","CAP_VERTEX",VERTEX,{"disambiguationData":[OSD([subQ1,subQ4])],"isStart":false})])]})]})])]})]}),makeQuery(id+"F6.opExtrude","SWEPT_FACE",FACE,{"disambiguationData":[OSD([subQ0]),TDD([makeQuery(id+"F3.boolean.opBoolean","SPLIT",EDGE,{"disambiguationData":[TD([subQ8])],"derivedFrom":subQ7})])]}),makeQuery(id+"F6.opExtrude","SWEPT_FACE",FACE,{"disambiguationData":[OSD([subQ1,subQ0]),TDD([makeQuery(id+"F4.boolean.opBoolean","MERGE",EDGE,{"derivedFrom":[makeQuery(id+"F3.boolean.opBoolean","SPLIT",EDGE,{"disambiguationData":[TD([subQ2])],"derivedFrom":subQ7}),makeQuery(id+"F4.opExtrude","SWEPT_EDGE",EDGE,{"disambiguationData":[OSD([subQ1,subQ0]),TDD([makeQuery(id+"F1.opExtrude","CAP_VERTEX",VERTEX,{"disambiguationData":[OSD([subQ1,subQ0])],"isStart":false})])]})]})])]})]});}
            var sketch = newSketch(context, id + "F9", { "sketchPlane" : qUnion([Q0])});
            skText(sketch, "E20", { "text": "Victor-CreatBot\n", "fontName": "OpenSans-Italic.ttf"});
            skText(sketch, "E21", { "text": "3D Printer", "fontName": "OpenSans-Italic.ttf"});
            skText(sketch, "E22", { "text": "and", "fontName": "OpenSans-Regular.ttf"});
            skText(sketch, "E23", { "text": "Laser Engraver", "fontName": "OpenSans-Italic.ttf"});
            skText(sketch, "E24", { "text": "Controller", "fontName": "OpenSans-Italic.ttf"});
            skText(sketch, "E25", { "text": "Proudly Singapore Made", "fontName": "OpenSans-Italic.ttf"});
            const initialGuessF9  = {"E20": [0.009, 0.08675, 1, 0, 0.01], "E21": [0.0307, 0.07375, 1, 0, 0.008], "E22": [0.044, 0.06075, 1, 0, 0.008], "E23": [0.019, 0.04775, 1, 0, 0.008], "E24": [0.0311, 0.03475, 1, 0, 0.008], "E25": [0.00056, 0.0078, 1, 0, 0.004]};
            skSetInitialGuess(sketch, initialGuessF9);
            skSolve(sketch);
        }
        {
            var Q0;
            Q0 = qSketchRegion(id + "F9", true);
            extrude(context, id + "F10", {"entities" : qUnion([Q0]), "operationType" : NewBodyOperationType.ADD, "depth" : 1.5 * mm, "offsetDistance" : 25 * mm});
        }
        {
            var Q0;
            {var subQ0=sQuery(id+"F0.wireOp",EDGE,"E0.left");var subQ1=sQuery(id+"F0.wireOp",EDGE,"E0.top");Q0=makeQuery(id+"F8.boolean.opBoolean","MERGE",FACE,{"derivedFrom":[makeQuery(id+"F5.boolean.opBoolean","MERGE",FACE,{"derivedFrom":[makeQuery(id+"F3.boolean.opBoolean","SPLIT",FACE,{"disambiguationData":[TD([makeQuery(id+"F1.opExtrude","SWEPT_FACE",FACE,{"disambiguationData":[OSD([subQ0])]})])],"derivedFrom":makeQuery(id+"F1.opExtrude","SWEPT_FACE",FACE,{"disambiguationData":[OSD([subQ1])]})}),makeQuery(id+"F5.opExtrude","SWEPT_FACE",FACE,{"disambiguationData":[OSD([subQ1,subQ0])]})]}),makeQuery(id+"F8.opExtrude","SWEPT_FACE",FACE,{"disambiguationData":[OSD([sQuery(id+"F7.wireOp",EDGE,"E12.bottom")])]})]});}
            var sketch = newSketch(context, id + "F11", { "sketchPlane" : qUnion([Q0])});
            skLineSegment(sketch, "E26.bottom", {"start": v(6, 2) * mm, "end": v(4.5, 2) * mm});
            skLineSegment(sketch, "E26.top", {"start": v(6, -7) * mm, "end": v(4.5, -7) * mm});
            skLineSegment(sketch, "E26.left", {"start": v(6, 2) * mm, "end": v(6, -7) * mm});
            skLineSegment(sketch, "E26.right", {"start": v(4.5, 2) * mm, "end": v(4.5, -7) * mm});
            skSolve(sketch);
        }
        {
            var Q0;
            {var subQ35=sQuery(id+"F11.wireOp",EDGE,"E26.bottom");Q0=makeQuery(id+"F11.imprint","IMPRINT",FACE,{"disambiguationData":[TD([[makeQuery(id+"F11.imprint","IMPRINT",EDGE,{"derivedFrom":subQ35}),1.0]])]});}
            extrude(context, id + "F12", {"entities" : qUnion([Q0]), "operationType" : NewBodyOperationType.ADD, "depth" : 10 * mm, "offsetDistance" : 25 * mm});
        }
        {
            var Q0;
            {var subQ0=sQuery(id+"F0.wireOp",EDGE,"E0.right");var subQ1=sQuery(id+"F0.wireOp",EDGE,"E0.top");Q0=makeQuery(id+"F8.boolean.opBoolean","MERGE",FACE,{"derivedFrom":[makeQuery(id+"F6.boolean.opBoolean","MERGE",FACE,{"derivedFrom":[makeQuery(id+"F3.boolean.opBoolean","SPLIT",FACE,{"disambiguationData":[TD([makeQuery(id+"F1.opExtrude","SWEPT_FACE",FACE,{"disambiguationData":[OSD([subQ0])]})])],"derivedFrom":makeQuery(id+"F1.opExtrude","SWEPT_FACE",FACE,{"disambiguationData":[OSD([subQ1])]})}),makeQuery(id+"F6.opExtrude","SWEPT_FACE",FACE,{"disambiguationData":[OSD([subQ1,subQ0])]})]}),makeQuery(id+"F8.opExtrude","SWEPT_FACE",FACE,{"disambiguationData":[OSD([sQuery(id+"F7.wireOp",EDGE,"E11.bottom")])]})]});}
            var sketch = newSketch(context, id + "F13", { "sketchPlane" : qUnion([Q0])});
            skLineSegment(sketch, "E27.bottom", {"start": v(-118.25, 2) * mm, "end": v(-116.75, 2) * mm});
            skLineSegment(sketch, "E27.top", {"start": v(-118.25, -7) * mm, "end": v(-116.75, -7) * mm});
            skLineSegment(sketch, "E27.left", {"start": v(-118.25, 2) * mm, "end": v(-118.25, -7) * mm});
            skLineSegment(sketch, "E27.right", {"start": v(-116.75, 2) * mm, "end": v(-116.75, -7) * mm});
            skSolve(sketch);
        }
        {
            var Q0;
            {var subQ35=sQuery(id+"F13.wireOp",EDGE,"E27.bottom");Q0=makeQuery(id+"F13.imprint","IMPRINT",FACE,{"disambiguationData":[TD([[makeQuery(id+"F13.imprint","IMPRINT",EDGE,{"derivedFrom":subQ35}),1.0]])]});}
            extrude(context, id + "F14", {"entities" : qUnion([Q0]), "operationType" : NewBodyOperationType.ADD, "depth" : 10 * mm, "offsetDistance" : 25 * mm});
        }
        {
            var Q0;
            Q0=makeQuery(id+"F14.opExtrude","CAP_EDGE",EDGE,{"disambiguationData":[OSD([sQuery(id+"F13.wireOp",EDGE,"E27.bottom")])],"isStart":false});
            var Q1;
            Q1=makeQuery(id+"F14.opExtrude","CAP_EDGE",EDGE,{"disambiguationData":[OSD([sQuery(id+"F13.wireOp",EDGE,"E27.top")])],"isStart":false});
            var Q2;
            Q2=makeQuery(id+"F12.opExtrude","CAP_EDGE",EDGE,{"disambiguationData":[OSD([sQuery(id+"F11.wireOp",EDGE,"E26.bottom")])],"isStart":false});
            var Q3;
            Q3=makeQuery(id+"F12.opExtrude","CAP_EDGE",EDGE,{"disambiguationData":[OSD([sQuery(id+"F11.wireOp",EDGE,"E26.top")])],"isStart":false});
            fillet(context, id + "F15", {"entities" : qUnion([Q0, Q1, Q2, Q3]), "radius" : 5 * mm, "tangentPropagation" : true, "allowEdgeOverflow" : false});
        }
        {
            var Q0;
            Q0=makeQuery(id+"F8.opExtrude","SWEPT_FACE",FACE,{"disambiguationData":[OSD([sQuery(id+"F7.wireOp",EDGE,"E13.bottom"),sQuery(id+"F7.wireOp",EDGE,"E14.trimOffspring")])]});
            var sketch = newSketch(context, id + "F16", { "sketchPlane" : qUnion([Q0])});
            skLineSegment(sketch, "E28.bottom", {"start": v(-112.8, -7) * mm, "end": v(-92.8, -7) * mm});
            skLineSegment(sketch, "E28.top", {"start": v(-112.8, -5) * mm, "end": v(-92.8, -5) * mm});
            skLineSegment(sketch, "E28.left", {"start": v(-112.8, -7) * mm, "end": v(-112.8, -5) * mm});
            skLineSegment(sketch, "E28.right", {"start": v(-92.8, -7) * mm, "end": v(-92.8, -5) * mm});
            skLineSegment(sketch, "E29.bottom", {"start": v(0, -7) * mm, "end": v(-20, -7) * mm});
            skLineSegment(sketch, "E29.top", {"start": v(0, -5) * mm, "end": v(-20, -5) * mm});
            skLineSegment(sketch, "E29.left", {"start": v(0, -7) * mm, "end": v(0, -5) * mm});
            skLineSegment(sketch, "E29.right", {"start": v(-20, -7) * mm, "end": v(-20, -5) * mm});
            skSolve(sketch);
        }
        {
            var Q0;
            {var subQ0=sQuery(id+"F0.wireOp",EDGE,"E0.right");Q0=makeQuery(id+"F14.boolean.opBoolean","MERGE",FACE,{"derivedFrom":[makeQuery(id+"F8.boolean.opBoolean","MERGE",FACE,{"derivedFrom":[makeQuery(id+"F6.opExtrude","CAP_FACE",FACE,{"disambiguationData":[OSD([subQ0])],"isStart":false}),makeQuery(id+"F6.opExtrude","CAP_FACE",FACE,{"disambiguationData":[OSD([sQuery(id+"F0.wireOp",EDGE,"E0.bottom"),subQ0])],"isStart":false}),makeQuery(id+"F8.opExtrude","SWEPT_FACE",FACE,{"disambiguationData":[OSD([sQuery(id+"F7.wireOp",EDGE,"E11.left"),sQuery(id+"F7.wireOp",EDGE,"E16.trimOffspring")])]})]}),makeQuery(id+"F14.opExtrude","SWEPT_FACE",FACE,{"disambiguationData":[OSD([sQuery(id+"F13.wireOp",EDGE,"E27.left")])]})]});}
            var sketch = newSketch(context, id + "F17", { "sketchPlane" : qUnion([Q0])});
            skCircle(sketch, "E30", {"center": v(112.75, -2) * mm, "radius": 1 * mm});
            skSolve(sketch);
        }
        {
            var Q0;
            Q0=makeQuery(id+"F17.imprint","IMPRINT",FACE,{"disambiguationData":[TD([[makeQuery(id+"F17.imprint","IMPRINT",EDGE,{"derivedFrom":sQuery(id+"F17.wireOp",EDGE,"E30")}),1.0]])]});
            extrude(context, id + "F18", {"entities" : qUnion([Q0]), "operationType" : NewBodyOperationType.REMOVE, "endBound" : BoundingType.THROUGH_ALL, "oppositeDirection" : true, "depth" : 25 * mm, "offsetDistance" : 25 * mm});
        }
        {
            var Q0;
            {var subQ0=sQuery(id+"F0.wireOp",EDGE,"E0.left");var subQ1=sQuery(id+"F0.wireOp",EDGE,"E0.bottom");Q0=makeQuery(id+"F5.boolean.opBoolean","MERGE",EDGE,{"derivedFrom":[makeQuery(id+"F4.opExtrude","CAP_EDGE",EDGE,{"disambiguationData":[OSD([subQ1]),TDD([makeQuery(id+"F3.boolean.opBoolean","SPLIT",EDGE,{"disambiguationData":[TD([makeQuery(id+"F1.opExtrude","SWEPT_FACE",FACE,{"disambiguationData":[OSD([subQ0])]})])],"derivedFrom":makeQuery(id+"F1.opExtrude","CAP_EDGE",EDGE,{"disambiguationData":[OSD([subQ1])],"isStart":false})})])],"isStart":false}),makeQuery(id+"F5.opExtrude","SWEPT_EDGE",EDGE,{"disambiguationData":[OSD([subQ1,subQ0]),TDD([makeQuery(id+"F4.opExtrude","CAP_VERTEX",VERTEX,{"disambiguationData":[OSD([subQ1,subQ0]),TDD([makeQuery(id+"F1.opExtrude","CAP_VERTEX",VERTEX,{"disambiguationData":[OSD([subQ1,subQ0])],"isStart":false})])],"isStart":false})])]})]});}
            var Q1;
            {var subQ0=sQuery(id+"F0.wireOp",EDGE,"E0.left");var subQ1=sQuery(id+"F0.wireOp",EDGE,"E0.bottom");Q1=makeQuery(id+"F5.opExtrude","CAP_EDGE",EDGE,{"disambiguationData":[OSD([subQ1,subQ0]),TDD([makeQuery(id+"F4.boolean.opBoolean","MERGE",EDGE,{"derivedFrom":[makeQuery(id+"F3.boolean.opBoolean","SPLIT",EDGE,{"disambiguationData":[TD([makeQuery(id+"F1.opExtrude","SWEPT_FACE",FACE,{"disambiguationData":[OSD([subQ1])]})])],"derivedFrom":makeQuery(id+"F1.opExtrude","CAP_EDGE",EDGE,{"disambiguationData":[OSD([subQ0])],"isStart":false})}),makeQuery(id+"F4.opExtrude","SWEPT_EDGE",EDGE,{"disambiguationData":[OSD([subQ1,subQ0]),TDD([makeQuery(id+"F1.opExtrude","CAP_VERTEX",VERTEX,{"disambiguationData":[OSD([subQ1,subQ0])],"isStart":false})])]})]})])],"isStart":false});}
            var Q2;
            {var subQ0=sQuery(id+"F0.wireOp",EDGE,"E0.left");var subQ1=sQuery(id+"F0.wireOp",EDGE,"E0.bottom");Q2=makeQuery(id+"F8.boolean.opBoolean","MERGE",EDGE,{"derivedFrom":[makeQuery(id+"F5.opExtrude","CAP_EDGE",EDGE,{"disambiguationData":[OSD([subQ1,subQ0]),TDD([makeQuery(id+"F4.opExtrude","CAP_EDGE",EDGE,{"disambiguationData":[OSD([subQ1,subQ0])],"isStart":false})])],"isStart":false}),makeQuery(id+"F8.opExtrude","SWEPT_EDGE",EDGE,{"disambiguationData":[OSD([sQuery(id+"F7.wireOp",EDGE,"E12.top"),sQuery(id+"F7.wireOp",EDGE,"E19.trimOffspring")])]})]});}
            var Q3;
            {var subQ0=sQuery(id+"F0.wireOp",EDGE,"E0.right");var subQ1=sQuery(id+"F0.wireOp",EDGE,"E0.bottom");Q3=makeQuery(id+"F8.boolean.opBoolean","MERGE",EDGE,{"derivedFrom":[makeQuery(id+"F6.opExtrude","CAP_EDGE",EDGE,{"disambiguationData":[OSD([subQ1,subQ0]),TDD([makeQuery(id+"F4.opExtrude","CAP_EDGE",EDGE,{"disambiguationData":[OSD([subQ1,subQ0])],"isStart":false})])],"isStart":false}),makeQuery(id+"F8.opExtrude","SWEPT_EDGE",EDGE,{"disambiguationData":[OSD([sQuery(id+"F7.wireOp",EDGE,"E11.top"),sQuery(id+"F7.wireOp",EDGE,"E16.trimOffspring")])]})]});}
            var Q4;
            {var subQ0=sQuery(id+"F0.wireOp",EDGE,"E0.right");var subQ1=sQuery(id+"F0.wireOp",EDGE,"E0.bottom");Q4=makeQuery(id+"F6.opExtrude","CAP_EDGE",EDGE,{"disambiguationData":[OSD([subQ1,subQ0]),TDD([makeQuery(id+"F4.boolean.opBoolean","MERGE",EDGE,{"derivedFrom":[makeQuery(id+"F3.boolean.opBoolean","SPLIT",EDGE,{"disambiguationData":[TD([makeQuery(id+"F1.opExtrude","SWEPT_FACE",FACE,{"disambiguationData":[OSD([subQ1])]})])],"derivedFrom":makeQuery(id+"F1.opExtrude","CAP_EDGE",EDGE,{"disambiguationData":[OSD([subQ0])],"isStart":false})}),makeQuery(id+"F4.opExtrude","SWEPT_EDGE",EDGE,{"disambiguationData":[OSD([subQ1,subQ0]),TDD([makeQuery(id+"F1.opExtrude","CAP_VERTEX",VERTEX,{"disambiguationData":[OSD([subQ1,subQ0])],"isStart":false})])]})]})])],"isStart":false});}
            var Q5;
            {var subQ0=sQuery(id+"F0.wireOp",EDGE,"E0.right");var subQ1=sQuery(id+"F0.wireOp",EDGE,"E0.bottom");Q5=makeQuery(id+"F6.boolean.opBoolean","MERGE",EDGE,{"derivedFrom":[makeQuery(id+"F4.opExtrude","CAP_EDGE",EDGE,{"disambiguationData":[OSD([subQ1]),TDD([makeQuery(id+"F3.boolean.opBoolean","SPLIT",EDGE,{"disambiguationData":[TD([makeQuery(id+"F1.opExtrude","SWEPT_FACE",FACE,{"disambiguationData":[OSD([subQ0])]})])],"derivedFrom":makeQuery(id+"F1.opExtrude","CAP_EDGE",EDGE,{"disambiguationData":[OSD([subQ1])],"isStart":false})})])],"isStart":false}),makeQuery(id+"F6.opExtrude","SWEPT_EDGE",EDGE,{"disambiguationData":[OSD([subQ1,subQ0]),TDD([makeQuery(id+"F4.opExtrude","CAP_VERTEX",VERTEX,{"disambiguationData":[OSD([subQ1,subQ0]),TDD([makeQuery(id+"F1.opExtrude","CAP_VERTEX",VERTEX,{"disambiguationData":[OSD([subQ1,subQ0])],"isStart":false})])],"isStart":false})])]})]});}
            fillet(context, id + "F19", {"entities" : qUnion([Q0, Q1, Q2, Q3, Q4, Q5]), "radius" : 2 * mm, "tangentPropagation" : true, "allowEdgeOverflow" : false});
        }
        {
            var Q0;
            {var subQ0=sQuery(id+"F0.wireOp",EDGE,"E0.left");var subQ1=sQuery(id+"F0.wireOp",EDGE,"E0.top");Q0=makeQuery(id+"F12.boolean.opBoolean","MERGE",EDGE,{"derivedFrom":[makeQuery(id+"F5.opExtrude","CAP_EDGE",EDGE,{"disambiguationData":[OSD([subQ0]),TDD([makeQuery(id+"F3.boolean.opBoolean","SPLIT",EDGE,{"disambiguationData":[TD([makeQuery(id+"F1.opExtrude","SWEPT_FACE",FACE,{"disambiguationData":[OSD([subQ1])]})])],"derivedFrom":makeQuery(id+"F1.opExtrude","CAP_EDGE",EDGE,{"disambiguationData":[OSD([subQ0])],"isStart":false})})])],"isStart":false}),makeQuery(id+"F12.opExtrude","SWEPT_EDGE",EDGE,{"disambiguationData":[OSD([sQuery(id+"F11.wireOp",EDGE,"E26.bottom"),sQuery(id+"F11.wireOp",EDGE,"E26.left")])]})]});}
            var Q1;
            {var subQ0=sQuery(id+"F0.wireOp",EDGE,"E0.right");var subQ1=sQuery(id+"F0.wireOp",EDGE,"E0.top");Q1=makeQuery(id+"F14.boolean.opBoolean","MERGE",EDGE,{"derivedFrom":[makeQuery(id+"F6.opExtrude","CAP_EDGE",EDGE,{"disambiguationData":[OSD([subQ0]),TDD([makeQuery(id+"F3.boolean.opBoolean","SPLIT",EDGE,{"disambiguationData":[TD([makeQuery(id+"F1.opExtrude","SWEPT_FACE",FACE,{"disambiguationData":[OSD([subQ1])]})])],"derivedFrom":makeQuery(id+"F1.opExtrude","CAP_EDGE",EDGE,{"disambiguationData":[OSD([subQ0])],"isStart":false})})])],"isStart":false}),makeQuery(id+"F14.opExtrude","SWEPT_EDGE",EDGE,{"disambiguationData":[OSD([sQuery(id+"F13.wireOp",EDGE,"E27.bottom"),sQuery(id+"F13.wireOp",EDGE,"E27.left")])]})]});}
            fillet(context, id + "F20", {"entities" : qUnion([Q0, Q1]), "radius" : 2 * mm, "rho" : 0.5, "crossSection" : FilletCrossSection.CONIC, "allowEdgeOverflow" : false});
        }
        {
            var Q0;
            Q0=makeQuery(id+"F16.imprint","IMPRINT",FACE,{"disambiguationData":[TD([[makeQuery(id+"F16.imprint","IMPRINT",EDGE,{"derivedFrom":sQuery(id+"F16.wireOp",EDGE,"E28.bottom")}),1.0]])]});
            var Q1;
            Q1=makeQuery(id+"F16.imprint","IMPRINT",FACE,{"disambiguationData":[TD([[makeQuery(id+"F16.imprint","IMPRINT",EDGE,{"derivedFrom":sQuery(id+"F16.wireOp",EDGE,"E29.bottom")}),1.0]])]});
            extrude(context, id + "F21", {"entities" : qUnion([Q0, Q1]), "operationType" : NewBodyOperationType.ADD, "depth" : 2 * mm, "offsetDistance" : 25 * mm});
        }
        {
            var Q0;
            Q0=makeQuery(id+"F21.opExtrude","CAP_EDGE",EDGE,{"disambiguationData":[OSD([sQuery(id+"F16.wireOp",EDGE,"E28.top")])],"isStart":false});
            var Q1;
            Q1=makeQuery(id+"F21.opExtrude","CAP_EDGE",EDGE,{"disambiguationData":[OSD([sQuery(id+"F16.wireOp",EDGE,"E28.bottom")])],"isStart":false});
            var Q2;
            Q2=makeQuery(id+"F21.opExtrude","CAP_EDGE",EDGE,{"disambiguationData":[OSD([sQuery(id+"F16.wireOp",EDGE,"E29.top")])],"isStart":false});
            var Q3;
            Q3=makeQuery(id+"F21.opExtrude","CAP_EDGE",EDGE,{"disambiguationData":[OSD([sQuery(id+"F16.wireOp",EDGE,"E29.bottom")])],"isStart":false});
            fillet(context, id + "F22", {"entities" : qUnion([Q0, Q1, Q2, Q3]), "radius" : 1 * mm, "tangentPropagation" : true, "allowEdgeOverflow" : false});
        }
    });
